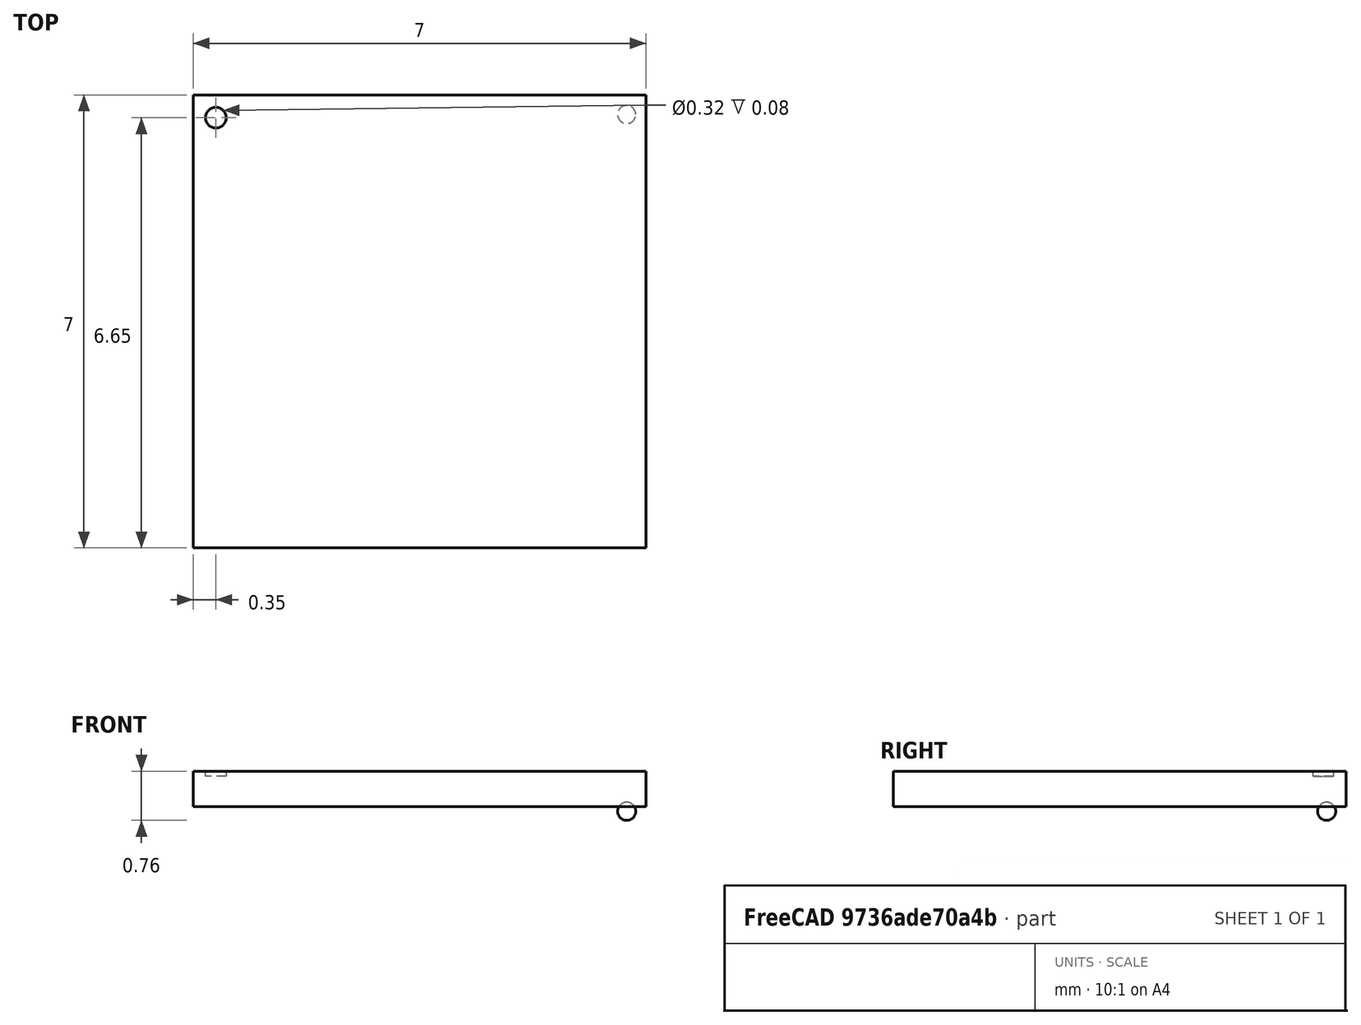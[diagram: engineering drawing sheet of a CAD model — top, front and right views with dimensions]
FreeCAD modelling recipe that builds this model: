
FCSTD DOCUMENT  (FreeCAD 0.20R29603 (Git))
Label: MIMXRT595SFFOC
License: All rights reserved
LicenseURL: http://en.wikipedia.org/wiki/All_rights_reserved
objects: Sketcher::SketchObject×2, PartDesign::Pad×1, Part::Sphere×1, Part::FeaturePython×1, PartDesign::Pocket×1, PartDesign::Body×1, App::Part×1
note: 8 computed .brp shape members not serialized (recipe doc carries the construction recipe); baked Part::Feature solids carry a one-line shape summary decoded from their .brp

FEATURE [Sketcher::SketchObject] Sketch  label="body_sk"
  FullyConstrained = true
  MapMode = 5
  Support = -> [XY_Plane]
  sketch-geometry (4):
    g0: LineSegment StartX=-3.5 StartY=3.5 StartZ=0 EndX=3.5 EndY=3.5 EndZ=0
    g1: LineSegment StartX=3.5 StartY=3.5 StartZ=0 EndX=3.5 EndY=-3.5 EndZ=0
    g2: LineSegment StartX=3.5 StartY=-3.5 StartZ=0 EndX=-3.5 EndY=-3.5 EndZ=0
    g3: LineSegment StartX=-3.5 StartY=-3.5 StartZ=0 EndX=-3.5 EndY=3.5 EndZ=0
  constraints (11):
    c: Coincident(g0,g1)
    c: Coincident(g1,g2)
    c: Coincident(g2,g3)
    c: Coincident(g3,g0)
    c: Horizontal(g0)
    c: Horizontal(g2)
    c: Vertical(g1)
    c: Vertical(g3)
    c: DistanceX(g0,g0) = 7
    c: DistanceY(g1,g1) = 7
    c: Symmetric(g1,g0,g-1)
FEATURE [PartDesign::Pad] Pad
  Direction = (0,0,1)
  Length = 0.55
  Length2 = 10
  Profile = -> Sketch
  ReferenceAxis = -> Sketch [N_Axis]
  Type = 0
FEATURE [Part::Sphere] Sphere
  Angle1 = -90
  Angle2 = 90
  Angle3 = 360
  AttacherType = Attacher::AttachEngine3D
  Placement = pos=(3.2,3.2,-0.07) rot=(0,0,1;0rad)
  Radius = 0.14
FEATURE [Part::FeaturePython] Array  label="Balls"  # Draft array (typed FeaturePython)
  AlwaysSyncPlacement = false
  Angle = 360
  ArrayType = 0
  Axis = (0,0,1)
  Base = -> Sphere
  Center = (0,0,0)
  Count = 289
  ExpandArray = false
  Fuse = false
  IntervalAxis = (0,0,0)
  IntervalX = (-0.4,0,0)
  IntervalY = (0,-0.4,0)
  IntervalZ = (0,0,0)
  NumberCircles = 3
  NumberPolar = 5
  NumberX = 17
  NumberY = 17
  NumberZ = 1
  PlacementList = 289 placements: [(3.2,3.2,-0.07),(3.2,2.8,-0.07),(3.2,2.4,-0.07),(3.2,2,-0.07),(3.2,1.6,-0.07),(3.2,1.2,-0.07),(3.2,0.8,-0.07),(3.2,0.4,-0.07),(3.2,0,-0.07),(3.2,-0.4,-0.07),(3.2,-0.8,-0.07),(3.2,-1.2,-0.07),(3.2,-1.6,-0.07),(3.2,-2,-0.07),(3.2,-2.4,-0.07),(3.2,-2.8,-0.07),(3.2,-3.2,-0.07),(2.8,3.2,-0.07),(2.8,2.8,-0.07),(2.8,2.4,-0.07),(2.8,2,-0.07),(2.8,1.6,-0.07),(2.8,1.2,-0.07),(2.8,0.8,-0.07),(2.8,0.4,-0.07),+264 more]
  RadialDistance = 50
  Symmetry = 1
  TangentialDistance = 25
FEATURE [Sketcher::SketchObject] Sketch001  label="mark_index_sk"
  FullyConstrained = true
  MapMode = 5
  Placement = pos=(0,0,0.55) rot=(0,0,1;0rad)
  Support = -> [Pad]
  sketch-geometry (1):
    g0: Circle CenterX=-3.15 CenterY=3.15 CenterZ=0 NormalX=0 NormalY=0 NormalZ=1 AngleXU=0 Radius=0.16
  constraints (3):
    c: Radius(g0) = 0.16
    c: DistanceY(g-1,g0) = 3.15
    c: DistanceX(g0,g-1) = 3.15
FEATURE [PartDesign::Pocket] Pocket
  BaseFeature = -> Pad
  Direction = (0,0,-1)
  Length = 0.08
  Length2 = 5
  Profile = -> Sketch001
  ReferenceAxis = -> Sketch001 [N_Axis]
  Type = 0
FEATURE [PartDesign::Body] Body  label="body"
  Group = -> [Sketch,Pad,Sketch001,Pocket]
  Origin = -> Origin
  Tip = -> Pocket
FEATURE [App::Part] Part
  Group = -> [Body,Sphere,Array]
  Origin = -> Origin001
